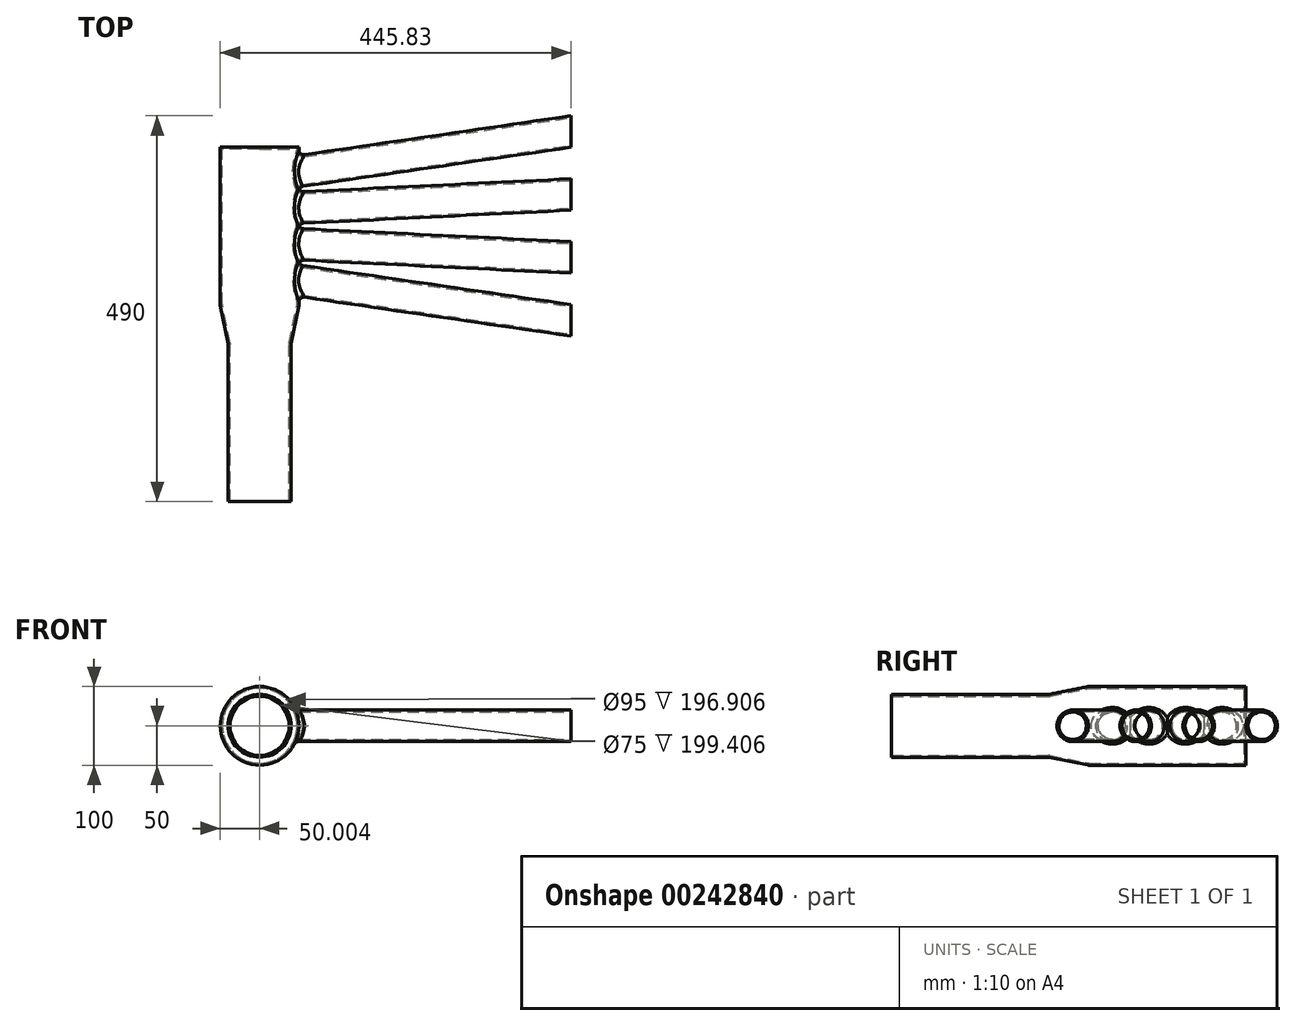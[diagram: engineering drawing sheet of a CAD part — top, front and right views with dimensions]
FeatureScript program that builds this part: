
annotation { "Feature Type Name" : "Feature", "Feature Type Description" : "" }
export const myFeature = defineFeature(function(context is Context, id is Id, definition is map)
    precondition{}
    {
        {
            var Q0;
            Q0=qCreatedBy(makeId("Top.planeOp"),FACE);
            var sketch = newSketch(context, id + "F0", { "sketchPlane" : qUnion([Q0])});
            skLineSegment(sketch, "E0", {"start": v(0, 40) * mm, "end": v(-350, 23) * mm});
            skLineSegment(sketch, "E1", {"start": v(0, 120) * mm, "end": v(-350, 69) * mm});
            skLineSegment(sketch, "E2", {"start": v(0, -40) * mm, "end": v(-350, -23) * mm});
            skLineSegment(sketch, "E3", {"start": v(0, -120) * mm, "end": v(-350, -69) * mm});
            skLineSegment(sketch, "E4", {"start": v(0, 0) * mm, "end": v(-415.08, 0) * mm, "construction": true});
            skSolve(sketch);
        }
        {
            var Q0;
            Q0=qCreatedBy(makeId("Right.planeOp"),FACE);
            var sketch = newSketch(context, id + "F1", { "sketchPlane" : qUnion([Q0])});
            skCircle(sketch, "E5", {"center": v(-120, 0) * mm, "radius": 20 * mm});
            skCircle(sketch, "E6", {"center": v(-40, 0) * mm, "radius": 20 * mm});
            skCircle(sketch, "E7", {"center": v(40, 0) * mm, "radius": 20 * mm});
            skCircle(sketch, "E8", {"center": v(120, 0) * mm, "radius": 20 * mm});
            skSolve(sketch);
        }
        {
            var Q0;
            Q0=makeQuery(id+"F1.imprint","IMPRINT",FACE,{"disambiguationData":[TD([[makeQuery(id+"F1.imprint","IMPRINT",EDGE,{"derivedFrom":sQuery(id+"F1.wireOp",EDGE,"E5")}),1.0]])]});
            var Q1;
            Q1=sQuery(id+"F0.wireOp",EDGE,"E3");
            sweep(context, id + "F2", {"profiles" : qUnion([Q0]), "path" : qUnion([Q1])});
        }
        {
            var Q0;
            Q0=makeQuery(id+"F1.imprint","IMPRINT",FACE,{"disambiguationData":[TD([[makeQuery(id+"F1.imprint","IMPRINT",EDGE,{"derivedFrom":sQuery(id+"F1.wireOp",EDGE,"E6")}),1.0]])]});
            var Q1;
            Q1=sQuery(id+"F0.wireOp",EDGE,"E2");
            sweep(context, id + "F3", {"profiles" : qUnion([Q0]), "path" : qUnion([Q1])});
        }
        {
            var Q0;
            Q0=makeQuery(id+"F1.imprint","IMPRINT",FACE,{"disambiguationData":[TD([[makeQuery(id+"F1.imprint","IMPRINT",EDGE,{"derivedFrom":sQuery(id+"F1.wireOp",EDGE,"E7")}),1.0]])]});
            var Q1;
            Q1=sQuery(id+"F0.wireOp",EDGE,"E0");
            sweep(context, id + "F4", {"profiles" : qUnion([Q0]), "path" : qUnion([Q1])});
        }
        {
            var Q0;
            Q0=makeQuery(id+"F1.imprint","IMPRINT",FACE,{"disambiguationData":[TD([[makeQuery(id+"F1.imprint","IMPRINT",EDGE,{"derivedFrom":sQuery(id+"F1.wireOp",EDGE,"E8")}),1.0]])]});
            var Q1;
            Q1=sQuery(id+"F0.wireOp",EDGE,"E1");
            sweep(context, id + "F5", {"profiles" : qUnion([Q0]), "path" : qUnion([Q1])});
        }
        {
            var Q0;
            Q0=qCreatedBy(makeId("Front.planeOp"),FACE);
            var sketch = newSketch(context, id + "F6", { "sketchPlane" : qUnion([Q0])});
            skCircle(sketch, "E9", {"center": v(-395.83, 0) * mm, "radius": 50 * mm});
            skLineSegment(sketch, "E10.0", {"start": v(-350, -20) * mm, "end": v(-350, 20) * mm, "construction": true});
            skSolve(sketch);
        }
        {
            var Q0;
            Q0 = qSketchRegion(id + "F6", true);
            extrude(context, id + "F7", {"entities" : qUnion([Q0]), "operationType" : NewBodyOperationType.ADD, "endBound" : BoundingType.SYMMETRIC, "depth" : 200 * mm});
        }
        {
            var Q0;
            Q0=makeQuery(id+"F7.opExtrude","CAP_FACE",FACE,{"disambiguationData":[OSD([sQuery(id+"F6.wireOp",EDGE,"E9")])],"isStart":false});
            cPlane(context, id + "F8", {"entities" : qUnion([Q0]), "cplaneType" : CPlaneType.OFFSET, "offset" : 50 * mm, "width" : 150 * mm, "height" : 150 * mm});
        }
        {
            var Q0;
            Q0=qCreatedBy(id+"F8.planeOp",FACE);
            var sketch = newSketch(context, id + "F9", { "sketchPlane" : qUnion([Q0])});
            skCircle(sketch, "E11", {"center": v(-395.83, 0) * mm, "radius": 40 * mm});
            skSolve(sketch);
        }
        {
            var Q0;
            Q0=makeQuery(id+"F7.opExtrude","CAP_FACE",FACE,{"disambiguationData":[OSD([sQuery(id+"F6.wireOp",EDGE,"E9")])],"isStart":false});
            var sketch = newSketch(context, id + "F10", { "sketchPlane" : qUnion([Q0])});
            skCircle(sketch, "E12.0", {"center": v(-395.83, 0) * mm, "radius": 50 * mm});
            skSolve(sketch);
        }
        {
            var Q1;
            Q1=makeQuery(id+"F10.imprint","IMPRINT",FACE,{"disambiguationData":[TD([[makeQuery(id+"F10.imprint","IMPRINT",EDGE,{"derivedFrom":sQuery(id+"F10.wireOp",EDGE,"E12.0")}),1.0]])]});
            var Q2;
            Q2=makeQuery(id+"F9.imprint","IMPRINT",FACE,{"disambiguationData":[TD([[makeQuery(id+"F9.imprint","IMPRINT",EDGE,{"derivedFrom":sQuery(id+"F9.wireOp",EDGE,"E11")}),1.0]])]});
            loft(context, id + "F11", {"operationType" : NewBodyOperationType.ADD, "sheetProfilesArray" : [{ "sheetProfileEntities" : qUnion([Q1]) }, { "sheetProfileEntities" : qUnion([Q2]) }]});
        }
        {
            var Q0;
            Q0=makeQuery(id+"F11.opLoft","CAP_FACE",FACE,{"disambiguationData":[OSD([makeQuery(id+"F9.imprint","IMPRINT",FACE,{"disambiguationData":[TD([[makeQuery(id+"F9.imprint","IMPRINT",EDGE,{"derivedFrom":sQuery(id+"F9.wireOp",EDGE,"E11")}),1.0]])]})])],"isStart":true});
            var sketch = newSketch(context, id + "F12", { "sketchPlane" : qUnion([Q0])});
            skCircle(sketch, "E13.0", {"center": v(-395.83, 0) * mm, "radius": 40 * mm});
            skSolve(sketch);
        }
        {
            var Q0;
            Q0 = qSketchRegion(id + "F12", true);
            extrude(context, id + "F13", {"entities" : qUnion([Q0]), "operationType" : NewBodyOperationType.ADD, "depth" : 200 * mm});
        }
        {
            var Q0;
            Q0=makeQuery(id+"F11.boolean.opBoolean","MERGE",EDGE,{"derivedFrom":[makeQuery(id+"F7.opExtrude","CAP_EDGE",EDGE,{"disambiguationData":[OSD([sQuery(id+"F6.wireOp",EDGE,"E9")])],"isStart":false}),makeQuery(id+"F11.opLoft","MID_CAP_EDGE",EDGE,{"disambiguationData":[OSD([sQuery(id+"F10.wireOp",EDGE,"E12.0")])],"capPos":0.0})]});
            var Q1;
            Q1=makeQuery(id+"F13.boolean.opBoolean","MERGE",EDGE,{"derivedFrom":[makeQuery(id+"F11.opLoft","MID_CAP_EDGE",EDGE,{"disambiguationData":[OSD([sQuery(id+"F9.wireOp",EDGE,"E11"),sQuery(id+"F10.wireOp",EDGE,"E12.0")])],"capPos":1.0}),makeQuery(id+"F13.opExtrude","CAP_EDGE",EDGE,{"disambiguationData":[OSD([sQuery(id+"F12.wireOp",EDGE,"E13.0")])],"isStart":true})]});
            var Q2;
            Q2=makeQuery(id+"F7.boolean.opBoolean","INTERSECT",EDGE,{"derivedFrom":[makeQuery(id+"F2.opSweep","SWEPT_FACE",FACE,{"disambiguationData":[OSD([sQuery(id+"F0.wireOp",EDGE,"E3"),sQuery(id+"F1.wireOp",EDGE,"E5")])]}),makeQuery(id+"F7.opExtrude","SWEPT_FACE",FACE,{"disambiguationData":[OSD([sQuery(id+"F6.wireOp",EDGE,"E9")])]})]});
            var Q3;
            Q3=makeQuery(id+"F7.boolean.opBoolean","INTERSECT",EDGE,{"derivedFrom":[makeQuery(id+"F3.opSweep","SWEPT_FACE",FACE,{"disambiguationData":[OSD([sQuery(id+"F0.wireOp",EDGE,"E2"),sQuery(id+"F1.wireOp",EDGE,"E6")])]}),makeQuery(id+"F7.opExtrude","SWEPT_FACE",FACE,{"disambiguationData":[OSD([sQuery(id+"F6.wireOp",EDGE,"E9")])]})]});
            var Q4;
            Q4=makeQuery(id+"F7.boolean.opBoolean","INTERSECT",EDGE,{"derivedFrom":[makeQuery(id+"F4.opSweep","SWEPT_FACE",FACE,{"disambiguationData":[OSD([sQuery(id+"F0.wireOp",EDGE,"E0"),sQuery(id+"F1.wireOp",EDGE,"E7")])]}),makeQuery(id+"F7.opExtrude","SWEPT_FACE",FACE,{"disambiguationData":[OSD([sQuery(id+"F6.wireOp",EDGE,"E9")])]})]});
            var Q5;
            Q5=makeQuery(id+"F7.boolean.opBoolean","INTERSECT",EDGE,{"derivedFrom":[makeQuery(id+"F5.opSweep","SWEPT_FACE",FACE,{"disambiguationData":[OSD([sQuery(id+"F0.wireOp",EDGE,"E1"),sQuery(id+"F1.wireOp",EDGE,"E8")])]}),makeQuery(id+"F7.opExtrude","SWEPT_FACE",FACE,{"disambiguationData":[OSD([sQuery(id+"F6.wireOp",EDGE,"E9")])]})]});
            fillet(context, id + "F14", {"entities" : qUnion([Q0, Q1, Q2, Q3, Q4, Q5]), "radius" : 6 * mm, "tangentPropagation" : true, "allowEdgeOverflow" : false});
        }
        {
            var Q0;
            Q0=makeQuery(id+"F13.opExtrude","CAP_FACE",FACE,{"disambiguationData":[OSD([sQuery(id+"F12.wireOp",EDGE,"E13.0")])],"isStart":false});
            var Q1;
            Q1=makeQuery(id+"F2.opSweep","CAP_FACE",FACE,{"disambiguationData":[OSD([sQuery(id+"F0.wireOp",VERTEX,"E3.start"),sQuery(id+"F1.wireOp",EDGE,"E5")])],"isStart":true});
            var Q2;
            Q2=makeQuery(id+"F3.opSweep","CAP_FACE",FACE,{"disambiguationData":[OSD([sQuery(id+"F0.wireOp",VERTEX,"E2.start"),sQuery(id+"F1.wireOp",EDGE,"E6")])],"isStart":true});
            var Q3;
            Q3=makeQuery(id+"F4.opSweep","CAP_FACE",FACE,{"disambiguationData":[OSD([sQuery(id+"F0.wireOp",VERTEX,"E0.start"),sQuery(id+"F1.wireOp",EDGE,"E7")])],"isStart":true});
            var Q4;
            Q4=makeQuery(id+"F5.opSweep","CAP_FACE",FACE,{"disambiguationData":[OSD([sQuery(id+"F0.wireOp",VERTEX,"E1.start"),sQuery(id+"F1.wireOp",EDGE,"E8")])],"isStart":true});
            shell(context, id + "F15", {"entities" : qUnion([Q0, Q1, Q2, Q3, Q4]), "thickness" : 2.5 * mm});
        }
    });
